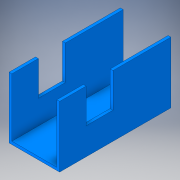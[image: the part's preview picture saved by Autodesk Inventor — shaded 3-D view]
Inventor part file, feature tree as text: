
AUTODESK INVENTOR PART (.ipt)
format: ipt  version: 2019 (Build 230136000, 136)  size: 170,496 bytes
history: native  units: mm
features: extrude x4, sketch x4, projected_geometry x4
ambient origin geometry x8: Origin, YZ Plane, XZ Plane, XY Plane, X Axis, Y Axis, Z Axis, Center Point
bodies: Solid1 (feature_tree)
feature tree (12):
  extrude  "Extrusion1"  Depth=124.08mm
  extrude  "Extrusion3"  Depth=10.0mm
  extrude  "Extrusion4"  Depth=3.18mm TaperAngle=0.0deg
  extrude  "Extrusion5"  Depth=3.18mm
  sketch  "Sketch1"  dims[d0=50.0mm d1=124.08mm]
  sketch  "Sketch4"  dims[d2=10.0mm d3=44.45mm]
  projected_geometry  "Projected Loop2"
  sketch  "Sketch5"  dims[d4=25.0mm d5=3.18mm d6=0.0mm]
  projected_geometry  "Projected Loop3"
  projected_geometry  "Projected Loop4"
  sketch  "Sketch6"  dims[d11=3.18mm d12=3.18mm d13=30.0mm d14=0.0mm d15=29.54mm d16=64.54mm d17=29.54mm d18=64.54mm d19=38.18mm d20=0.0mm d21=29.54mm d22=64.54mm d23=38.18mm d24=0.0mm]
  projected_geometry  "Projected Loop5"
